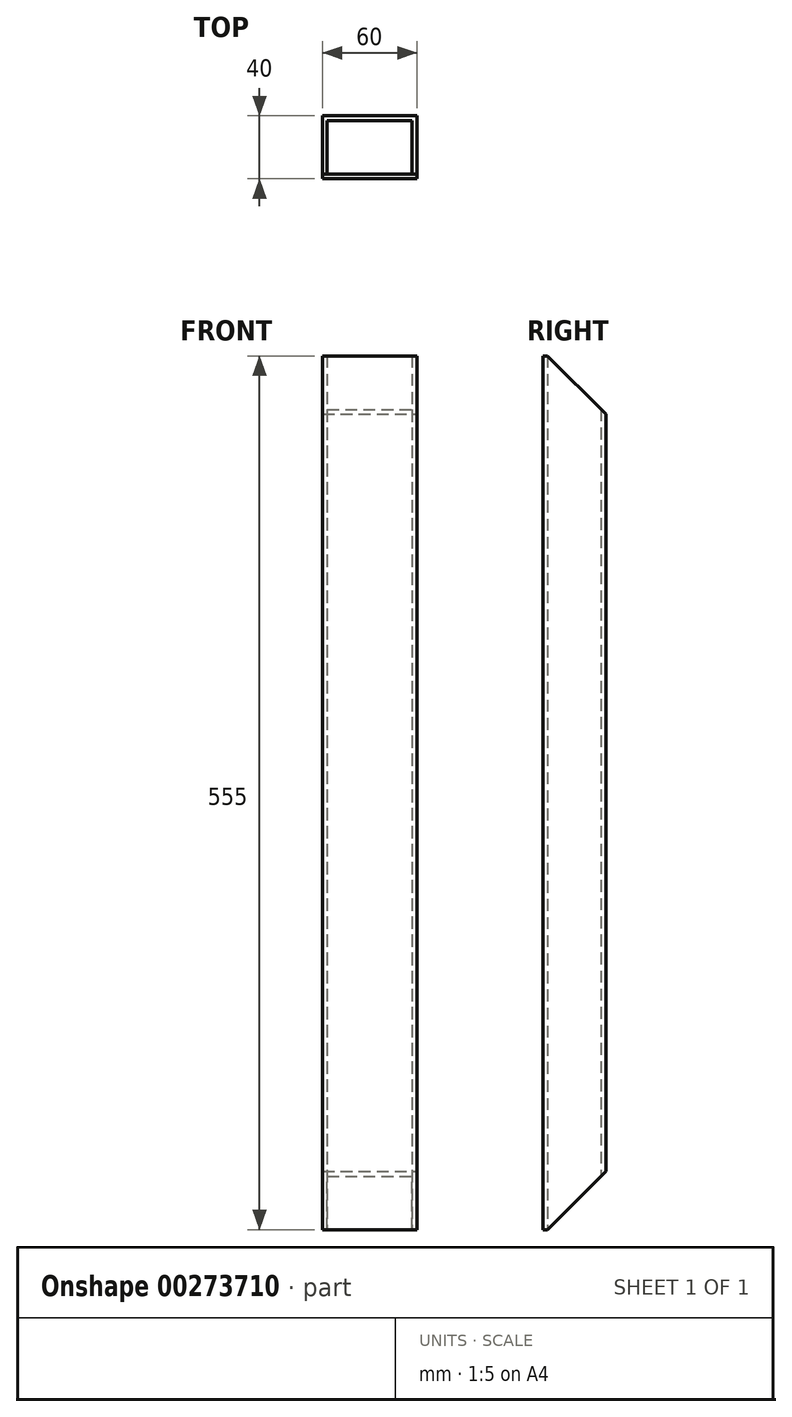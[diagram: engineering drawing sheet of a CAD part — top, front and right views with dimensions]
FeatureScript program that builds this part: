
annotation { "Feature Type Name" : "Feature", "Feature Type Description" : "" }
export const myFeature = defineFeature(function(context is Context, id is Id, definition is map)
    precondition{}
    {
        {
            var Q0;
            Q0=qCreatedBy(makeId("Top.planeOp"),FACE);
            var sketch = newSketch(context, id + "F0", { "sketchPlane" : qUnion([Q0])});
            skLineSegment(sketch, "E0.bottom", {"start": v(30, 20) * mm, "end": v(-30, 20) * mm});
            skLineSegment(sketch, "E0.top", {"start": v(30, -20) * mm, "end": v(-30, -20) * mm});
            skLineSegment(sketch, "E0.left", {"start": v(30, 20) * mm, "end": v(30, -20) * mm});
            skLineSegment(sketch, "E0.right", {"start": v(-30, 20) * mm, "end": v(-30, -20) * mm});
            skPoint(sketch, "E0.middle", {"position": v(0, 0) * mm});
            skLineSegment(sketch, "E1.bottom", {"start": v(27, 17) * mm, "end": v(-27, 17) * mm});
            skLineSegment(sketch, "E1.top", {"start": v(27, -17) * mm, "end": v(-27, -17) * mm});
            skLineSegment(sketch, "E1.left", {"start": v(27, 17) * mm, "end": v(27, -17) * mm});
            skLineSegment(sketch, "E1.right", {"start": v(-27, 17) * mm, "end": v(-27, -17) * mm});
            skSolve(sketch);
        }
        {
            var Q0;
            Q0=makeQuery(id+"F0.imprint","IMPRINT",FACE,{"disambiguationData":[TD([[makeQuery(id+"F0.imprint","IMPRINT",EDGE,{"derivedFrom":sQuery(id+"F0.wireOp",EDGE,"E0.bottom")}),1.0]])]});
            extrude(context, id + "F1", {"entities" : qUnion([Q0]), "depth" : 555 * mm});
        }
        {
            var Q0;
            Q0=makeQuery(id+"F1.opExtrude","SWEPT_FACE",FACE,{"disambiguationData":[OSD([sQuery(id+"F0.wireOp",EDGE,"E0.left")])]});
            var sketch = newSketch(context, id + "F2", { "sketchPlane" : qUnion([Q0])});
            skPoint(sketch, "E2", {"position": v(20, 518) * mm});
            skPoint(sketch, "E3", {"position": v(-17, 555) * mm});
            skLineSegment(sketch, "E4", {"start": v(-17, 555) * mm, "end": v(20, 518) * mm});
            skLineSegment(sketch, "E5", {"start": v(20, 555) * mm, "end": v(20, 518) * mm});
            skLineSegment(sketch, "E6", {"start": v(20, 555) * mm, "end": v(-17, 555) * mm});
            skPoint(sketch, "E7", {"position": v(-17, 0) * mm});
            skLineSegment(sketch, "E8", {"start": v(20, 0) * mm, "end": v(-17, 0) * mm});
            skPoint(sketch, "E9", {"position": v(20, 37) * mm});
            skLineSegment(sketch, "E10", {"start": v(-17, 0) * mm, "end": v(20, 37) * mm});
            skLineSegment(sketch, "E11", {"start": v(20, 0) * mm, "end": v(20, 37) * mm});
            skSolve(sketch);
        }
        {
            var Q0;
            Q0 = qSketchRegion(id + "F2", true);
            var Q1;
            Q1=makeQuery(id+"F2.imprint","IMPRINT",FACE,{"disambiguationData":[TD([[makeQuery(id+"F2.imprint","IMPRINT",EDGE,{"derivedFrom":sQuery(id+"F2.wireOp",EDGE,"E4")}),1.0]])]});
            extrude(context, id + "F3", {"entities" : qUnion([Q0, Q1]), "operationType" : NewBodyOperationType.REMOVE, "oppositeDirection" : true, "depth" : 60 * mm});
        }
        {
            var Q0;
            Q0=makeQuery(id+"F2.imprint","IMPRINT",FACE,{"disambiguationData":[TD([[makeQuery(id+"F2.imprint","IMPRINT",EDGE,{"derivedFrom":sQuery(id+"F2.wireOp",EDGE,"E8")}),-1.0]])]});
            extrude(context, id + "F4", {"entities" : qUnion([Q0]), "operationType" : NewBodyOperationType.REMOVE, "oppositeDirection" : true, "depth" : 60 * mm});
        }
    });
